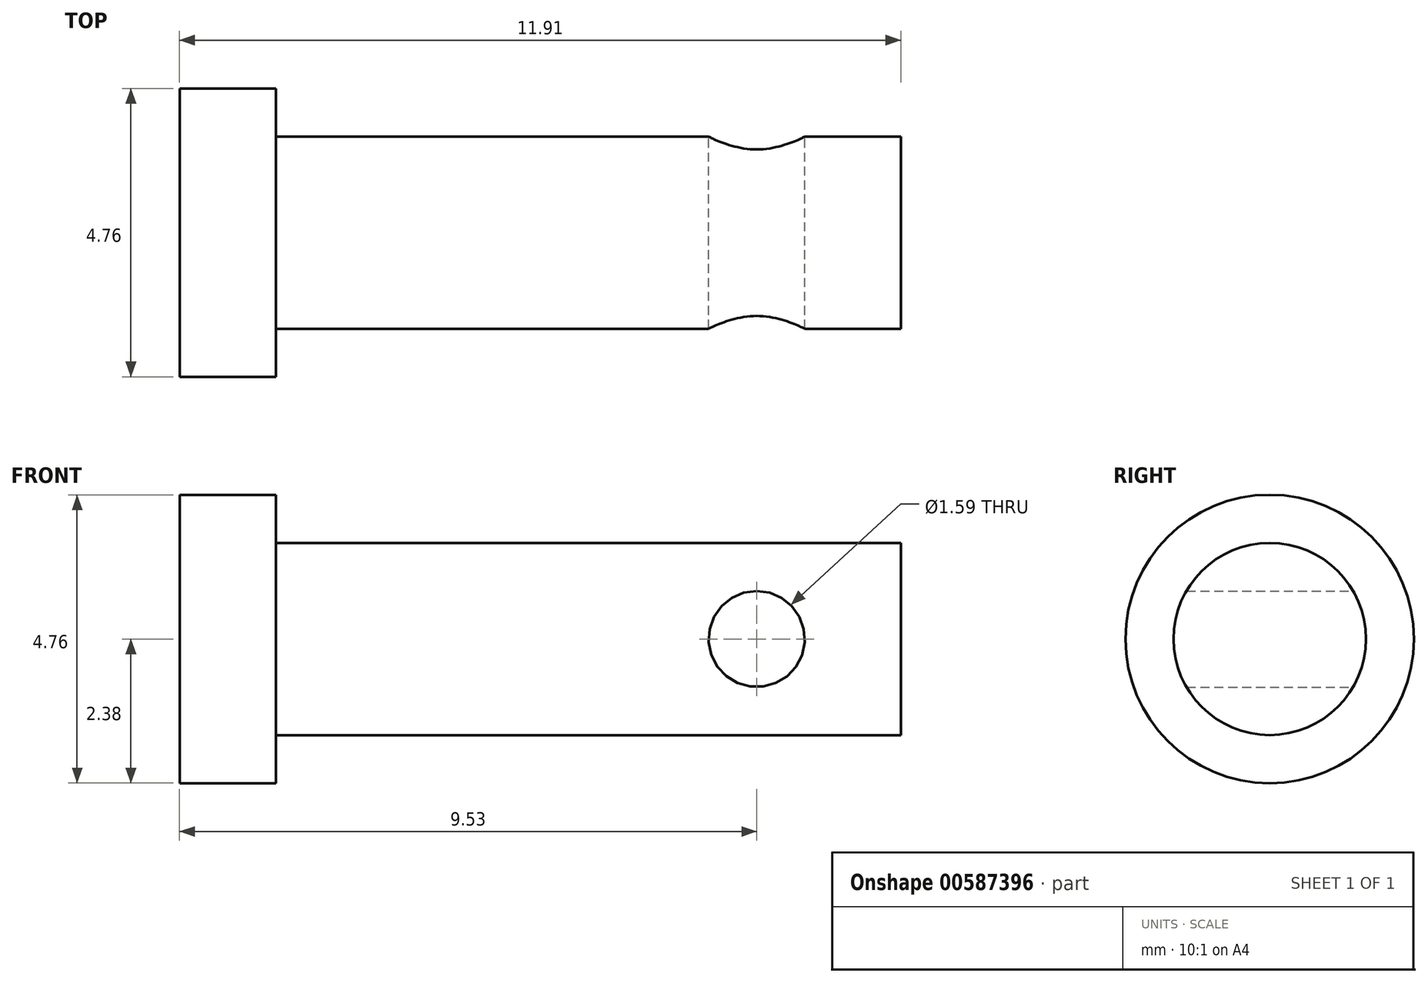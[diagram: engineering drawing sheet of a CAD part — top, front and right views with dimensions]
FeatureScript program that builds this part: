
annotation { "Feature Type Name" : "Feature", "Feature Type Description" : "" }
export const myFeature = defineFeature(function(context is Context, id is Id, definition is map)
    precondition{}
    {
        {
            var Q0;
            Q0=qCreatedBy(makeId("Front.planeOp"),FACE);
            var sketch = newSketch(context, id + "F0", { "sketchPlane" : qUnion([Q0])});
            skLineSegment(sketch, "E0", {"start": v(-7.94, 1.59) * mm, "end": v(2.38, 1.59) * mm});
            skLineSegment(sketch, "E1", {"start": v(2.38, 1.59) * mm, "end": v(2.38, 0) * mm});
            skLineSegment(sketch, "E2", {"start": v(-9.53, 2.38) * mm, "end": v(-7.94, 2.38) * mm});
            skLineSegment(sketch, "E3", {"start": v(-7.94, 2.38) * mm, "end": v(-7.94, 1.59) * mm});
            skLineSegment(sketch, "E4", {"start": v(5.4, 0) * mm, "end": v(-14.63, 0) * mm, "construction": true});
            skPoint(sketch, "E4.startSnap0", {"position": v(2.38, 0) * mm});
            skPoint(sketch, "E5.end.orphan", {"position": v(-7.94, -1.21) * mm});
            skPoint(sketch, "E6.orphan", {"position": v(2.38, -1.59) * mm});
            skLineSegment(sketch, "E7", {"start": v(2.38, 0) * mm, "end": v(-9.53, 0) * mm});
            skLineSegment(sketch, "E8", {"start": v(-9.53, 0) * mm, "end": v(-9.53, 2.38) * mm});
            skSolve(sketch);
        }
        {
            var Q0;
            Q0=makeQuery(id+"F0.imprint","IMPRINT",FACE,{"disambiguationData":[TD([[makeQuery(id+"F0.imprint","IMPRINT",EDGE,{"derivedFrom":sQuery(id+"F0.wireOp",EDGE,"E0")}),-1.0]])]});
            var Q1;
            Q1=sQuery(id+"F0.wireOp",EDGE,"E7");
            revolve(context, id + "F1", {"entities" : qUnion([Q0]), "axis" : qUnion([Q1]), "revolveType" : RevolveType.FULL});
        }
        {
            var Q0;
            Q0=qCreatedBy(makeId("Front.planeOp"),FACE);
            var sketch = newSketch(context, id + "F2", { "sketchPlane" : qUnion([Q0])});
            skCircle(sketch, "E9", {"center": v(0, 0) * mm, "radius": 0.8 * mm});
            skSolve(sketch);
        }
        {
            var Q0;
            Q0 = qSketchRegion(id + "F2", true);
            extrude(context, id + "F3", {"entities" : qUnion([Q0]), "operationType" : NewBodyOperationType.REMOVE, "endBound" : BoundingType.THROUGH_ALL, "depth" : 25.4 * mm, "offsetDistance" : 25.4 * mm, "hasSecondDirection" : true, "secondDirectionOppositeDirection" : true, "secondDirectionDepth" : 25.4 * mm});
        }
    });
